# Revit family: Haworth_Worksurface_Supports
name_source: partatom
category: Furniture Systems
revit_build: Autodesk Revit 2018 (Build: 20170223_1515(x64)
units: mm (PartAtom-declared; Revit-internal decimal feet)

## family parameters
Always vertical = Yes
Cut with Voids When Loaded = No
OmniClass Number = 23.40.70.14.64.21
OmniClass Title = Systems Furniture
Part Type = Normal
Room Calculation Point = No
Round Connector Dimension = Use Diameter
Shared = No
Work Plane-Based = No

## types (1)
- Support
    Actual Depth = 30"
    Actual Height = 29"
    Actual Width = 6"
    Assembly Code = E2020200
    Cantilever Bracket = No
    Cantilever Bracket Location = 1 3/4"
    Custom Size = Yes
    Depth = 30"
    Description = Haworth - Worksurface - Supports
    Double Support Leg = Yes
    End Support Location = 1 3/4"
    Height = 29"
    Manufacturer = Haworth
    Max. Depth = 36"
    Max. Height = 48"
    Max. Width = 120"
    Min. Depth = 18"
    Min. Height = 24"
    Min. Width = 6"
    Min/Max Depth = 18-36 in.
    Model = Haworth Worksurface Supports
    Revision Number = 1
    Size = Verify Final Dim. w/ Haworth
    Support Column = No
    Support Finish = Haworth _ Paint _ Metallic Champagne
    Support Height = 27 13/16"
    Support P Leg = No
    Support Panel = No
    Support Post_45 Degree = No
    Support Post_90 Degree = No
    Sustainability Info = http://www.haworth.com
    Table Thickness = 1 3/16"
    URL = www.haworth.com
    URL - Product = http://www.haworth.com
    Warranty = http://www.haworth.com
    Width = 1 1/2"

## geometry (parser evidence)
native form markers: Sweep x6
no freeform markers — native parametric forms only
